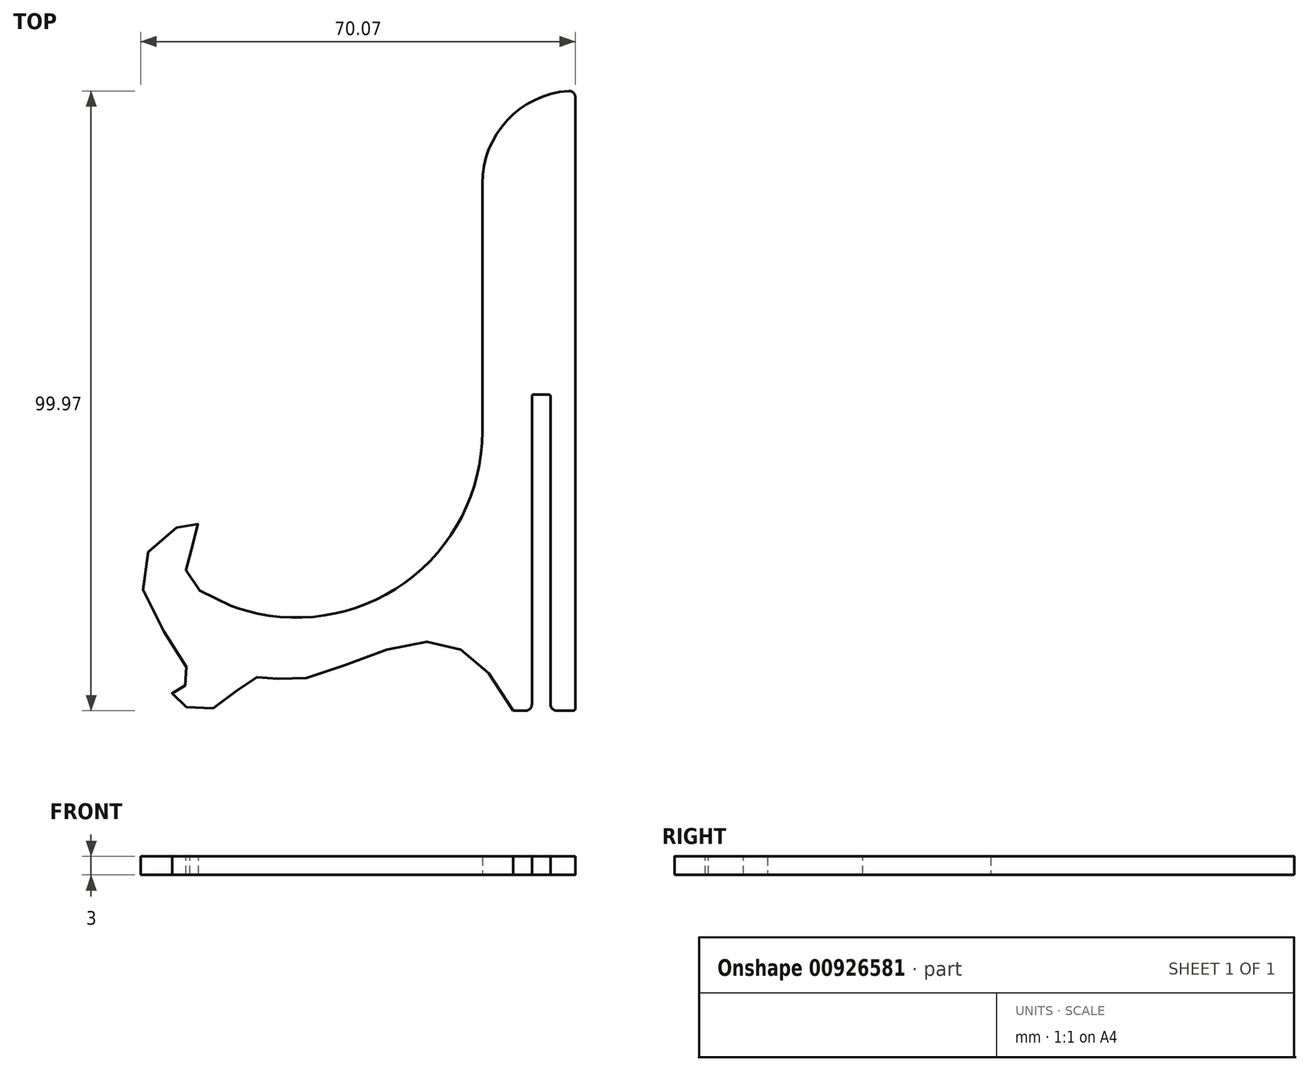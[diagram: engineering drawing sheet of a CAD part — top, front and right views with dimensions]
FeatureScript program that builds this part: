
annotation { "Feature Type Name" : "Feature", "Feature Type Description" : "" }
export const myFeature = defineFeature(function(context is Context, id is Id, definition is map)
    precondition{}
    {
        {
            var Q0;
            Q0=qCreatedBy(makeId("Top.planeOp"),FACE);
            var sketch = newSketch(context, id + "F0", { "sketchPlane" : qUnion([Q0])});
            skLineSegment(sketch, "E0", {"start": v(0, 0.3) * mm, "end": v(0, 98.96) * mm});
            skLineSegment(sketch, "E1", {"start": v(-15, 85) * mm, "end": v(-15, 45) * mm});
            skLineSegment(sketch, "E2", {"start": v(-4, 50.7) * mm, "end": v(-4, 1) * mm});
            skLineSegment(sketch, "E3", {"start": v(-7, 50.7) * mm, "end": v(-7, 1) * mm});
            skArc(sketch, "E4", {"start": v(-55.48, 16.89) * mm, "mid": v(-27.89, 20.36) * mm, "end": v(-15, 45) * mm});
            skLineSegment(sketch, "E5", {"start": v(-0.3, 0) * mm, "end": v(-3, 0) * mm});
            skFitSpline(sketch, "E6", {"points": [v(-10, 0) * mm, v(-23.84, 11.12) * mm, v(-45, 5) * mm, v(-51.95, 5.2) * mm, v(-60, 0) * mm, v(-65, 2.96) * mm, v(-62.2, 4.82) * mm, v(-70, 22.85) * mm, v(-60.94, 30.16) * mm, v(-62.8, 23.33) * mm, v(-54.58, 16.57) * mm], "startDerivative": vector(-87.8, 161.53) * mm, "endDerivative": vector(149.44, -51.66) * mm});
            skPoint(sketch, "E7.trimOffspring.end.orphan", {"position": v(-15, 0) * mm});
            skArc(sketch, "E8", {"start": v(-1.07, 99.96) * mm, "mid": v(-2.15, 99.85) * mm, "end": v(-3.21, 99.65) * mm});
            skPoint(sketch, "E9.orphan", {"position": v(0, 112.49) * mm});
            skArc(sketch, "E10.trimOffspring", {"start": v(-8.57, 97.3) * mm, "mid": v(-13.3, 91.94) * mm, "end": v(-15, 85) * mm});
            skPoint(sketch, "E11.visualSharp", {"position": v(0, 100) * mm});
            skArc(sketch, "E11.filletArc", {"start": v(0, 98.96) * mm, "mid": v(-0.32, 99.7) * mm, "end": v(-1.07, 99.96) * mm});
            skPoint(sketch, "E12.visualSharp", {"position": v(0, 0) * mm});
            skArc(sketch, "E12.filletArc", {"start": v(-0.3, 0) * mm, "mid": v(-0.09, 0.09) * mm, "end": v(0, 0.3) * mm});
            skArc(sketch, "E13", {"start": v(-8.57, 97.3) * mm, "mid": v(-6, 98.74) * mm, "end": v(-3.21, 99.65) * mm});
            skLineSegment(sketch, "E14", {"start": v(-6.7, 51) * mm, "end": v(-4.3, 51) * mm});
            skLineSegment(sketch, "E15.trimOffspring", {"start": v(-8, 0) * mm, "end": v(-10, 0) * mm});
            skPoint(sketch, "E16.visualSharp", {"position": v(-7, 51) * mm});
            skArc(sketch, "E16.filletArc", {"start": v(-6.7, 51) * mm, "mid": v(-6.91, 50.91) * mm, "end": v(-7, 50.7) * mm});
            skPoint(sketch, "E17.visualSharp", {"position": v(-4, 51) * mm});
            skArc(sketch, "E17.filletArc", {"start": v(-4, 50.7) * mm, "mid": v(-4.09, 50.91) * mm, "end": v(-4.3, 51) * mm});
            skPoint(sketch, "E18.visualSharp", {"position": v(-7, 0) * mm});
            skArc(sketch, "E18.filletArc", {"start": v(-8, 0) * mm, "mid": v(-7.3, 0.3) * mm, "end": v(-7, 1) * mm});
            skPoint(sketch, "E19.visualSharp", {"position": v(-4, 0) * mm});
            skArc(sketch, "E19.filletArc", {"start": v(-4, 1) * mm, "mid": v(-3.7, 0.3) * mm, "end": v(-3, 0) * mm});
            skSolve(sketch);
        }
        {
            var Q0;
            Q0=qSketchRegion(id+"F0",true);
            extrude(context, id + "F1", {"entities" : qUnion([Q0]), "depth" : 3 * mm, "offsetDistance" : 25 * mm});
        }
    });
